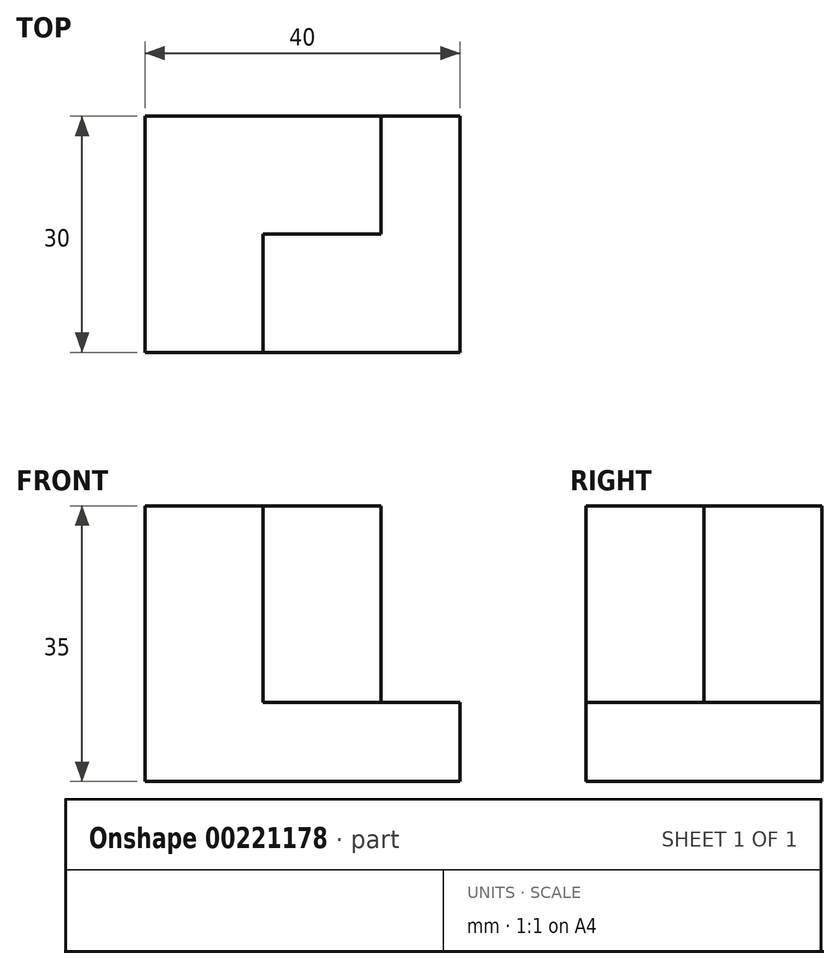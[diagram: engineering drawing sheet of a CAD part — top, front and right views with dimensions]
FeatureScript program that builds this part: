
annotation { "Feature Type Name" : "Feature", "Feature Type Description" : "" }
export const myFeature = defineFeature(function(context is Context, id is Id, definition is map)
    precondition{}
    {
        {
            var Q0;
            Q0=qCreatedBy(makeId("Front.planeOp"),FACE);
            var sketch = newSketch(context, id + "F0", { "sketchPlane" : qUnion([Q0])});
            skLineSegment(sketch, "E0", {"start": v(0, 0) * mm, "end": v(40, 0) * mm});
            skLineSegment(sketch, "E1", {"start": v(40, 0) * mm, "end": v(40, 10) * mm});
            skLineSegment(sketch, "E2", {"start": v(40, 10) * mm, "end": v(15, 10) * mm});
            skLineSegment(sketch, "E3", {"start": v(15, 10) * mm, "end": v(15, 35) * mm});
            skLineSegment(sketch, "E4", {"start": v(15, 35) * mm, "end": v(0, 35) * mm});
            skLineSegment(sketch, "E5", {"start": v(0, 35) * mm, "end": v(0, 0) * mm});
            skSolve(sketch);
        }
        {
            var Q0;
            Q0=makeQuery(id+"F0.imprint","IMPRINT",FACE,{"disambiguationData":[TD([[makeQuery(id+"F0.imprint","IMPRINT",EDGE,{"derivedFrom":sQuery(id+"F0.wireOp",EDGE,"E0")}),1.0]])]});
            extrude(context, id + "F1", {"entities" : qUnion([Q0]), "endBound" : BoundingType.SYMMETRIC, "depth" : 30 * mm});
        }
        {
            var Q0;
            Q0=qCreatedBy(makeId("Front.planeOp"),FACE);
            var sketch = newSketch(context, id + "F2", { "sketchPlane" : qUnion([Q0])});
            skLineSegment(sketch, "E6.0", {"start": v(15, 10) * mm, "end": v(15, 35) * mm});
            skLineSegment(sketch, "E7.0", {"start": v(30, 10) * mm, "end": v(15, 10) * mm});
            skLineSegment(sketch, "E8", {"start": v(15, 35) * mm, "end": v(30, 35) * mm});
            skLineSegment(sketch, "E9", {"start": v(30, 35) * mm, "end": v(30, 10) * mm});
            skPoint(sketch, "E10.orphan", {"position": v(40, 10) * mm});
            skSolve(sketch);
        }
        {
            var Q0;
            Q0=makeQuery(id+"F2.imprint","IMPRINT",FACE,{"disambiguationData":[TD([[makeQuery(id+"F2.imprint","IMPRINT",EDGE,{"derivedFrom":sQuery(id+"F2.wireOp",EDGE,"E6.0")}),-1.0]])]});
            extrude(context, id + "F3", {"entities" : qUnion([Q0]), "operationType" : NewBodyOperationType.ADD, "oppositeDirection" : true, "depth" : 15 * mm});
        }
    });
